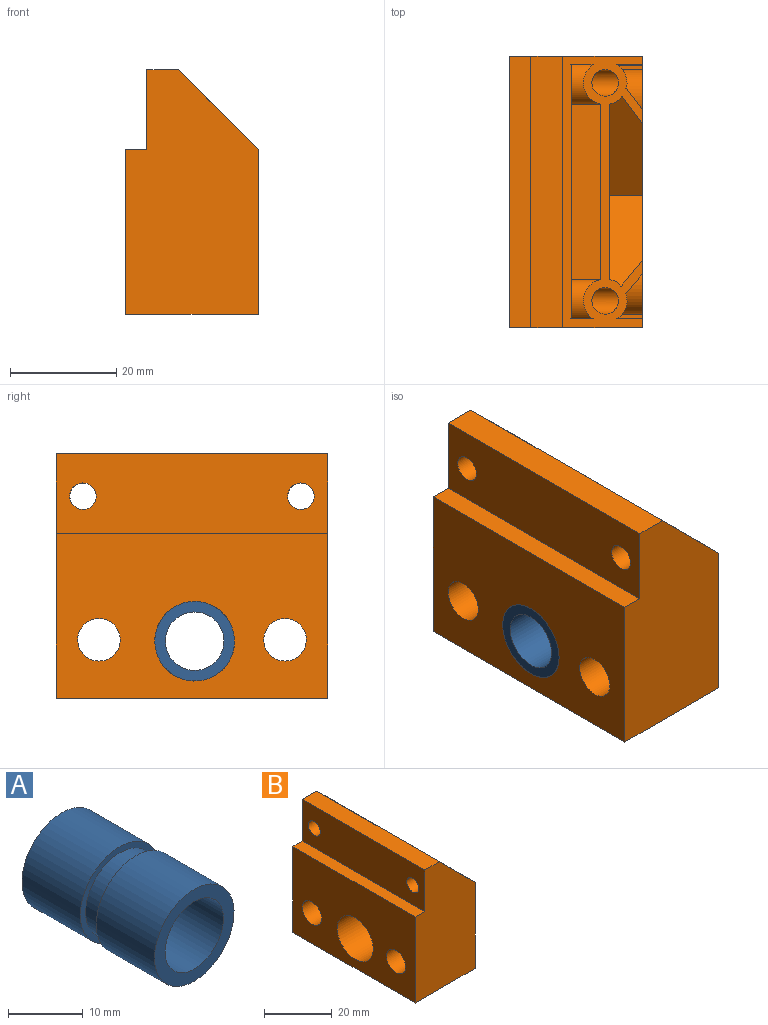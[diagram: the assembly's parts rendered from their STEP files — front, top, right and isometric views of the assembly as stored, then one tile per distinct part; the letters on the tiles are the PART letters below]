
ASSEMBLY  parts=2 mates=1
PART A: 8 faces, bbox 15x25x15 mm
  f0: cylinder r=7.5mm len=15mm, axis (0,1,0), area 518.4mm2, adj f1,f2
  f1: plane 15x15mm, normal (0,-1,0), area 44mm2, adj f0,f3
  f2: plane 15x15mm, normal (0,1,0), area 81.7mm2, adj f0,f7
  f3: cylinder r=6.5mm len=13mm, axis (0,1,0), area 122.5mm2, adj f1,f6
  f4: cylinder r=7.5mm len=15mm, axis (0,1,0), area 518.4mm2, adj f5,f6
  f5: plane 15x15mm, normal (0,-1,0), area 81.7mm2, adj f4,f7
  f6: plane 15x15mm, normal (0,1,0), area 44mm2, adj f3,f4
  f7: cylinder r=5.5mm len=25mm, axis (0,-1,0), area 863.9mm2, adj f2,f5
PART B: 77 faces, bbox 26.1x52.1x47.1 mm
  f0: plane 46x25mm, normal (0,1,0), area 977.5mm2, adj f1,f42,f43,f44,f48,f49,f69
  f1: plane 51x6mm, normal (0,0,1), area 306mm2, adj f0,f4,f48,f69
  f2: cylinder r=4.1mm len=16.5mm, axis (-1,0,0), area 85.8mm2, adj f8,f14,f51,f69
  f3: cylinder r=4.1mm len=16.5mm, axis (-1,0,0), area 80.5mm2, adj f7,f12,f22,f69
  f4: plane 46x25mm, normal (0,-1,0), area 977.5mm2, adj f1,f42,f43,f44,f48,f49,f69
  f5: cylinder r=2.5mm len=16.51mm, axis (-1,0,0), area 221.3mm2, adj f48,f69
  f6: cylinder r=2.5mm len=16.51mm, axis (-1,0,0), area 221.3mm2, adj f48,f69
  f7: plane 24.13x23.4mm, normal (0,-1,0), area 528.2mm2, adj f3,f16,f18,f22,f43,f66,f69
  f8: plane 24x23.4mm, normal (0,1,0), area 525.3mm2, adj f2,f17,f19,f43,f51,f64,f69
  f9: cylinder r=4.1mm len=15.41mm, axis (-1,0,0), area 36.8mm2, adj f11,f15,f21,f69
  f10: cylinder r=4.1mm len=15.57mm, axis (-1,0,0), area 40.5mm2, adj f11,f13,f21,f69
  f11: plane 32.96x13.2mm, normal (0,0,-1), area 435mm2, adj f9,f10,f21,f69
  f12: plane 23.4x18.93mm, normal (0,0.6,-0.8), area 515.6mm2, adj f3,f16,f18,f22,f43,f68,f69
  f13: plane 23.4x18.6mm, normal (0,-0.6,0.8), area 496.1mm2, adj f10,f15,f21,f32,f43,f52,f69
  f14: plane 23.4x17.16mm, normal (0,-0.64,-0.77), area 484.8mm2, adj f2,f17,f19,f43,f51,f67,f69
  f15: plane 23.4x17.01mm, normal (0,0.64,0.77), area 470.2mm2, adj f9,f13,f21,f32,f43,f52,f69
  f16: plane 23.34x18.15mm, normal (1,0,0), area 264.3mm2, adj f7,f12,f18,f20,f37,f62,f66,f68
  f17: plane 21.88x17.69mm, normal (1,0,0), area 247.1mm2, adj f8,f14,f19,f33,f34,f59,f64,f67
  f18: plane 10.57x4mm, normal (0,0,-1), area 42.3mm2, adj f7,f12,f16,f22
  f19: plane 10.41x4mm, normal (0,0,-1), area 41.6mm2, adj f8,f14,f17,f51
  f20: cylinder r=9.1mm len=23.4mm, axis (-1,0,0), area 296.6mm2, adj f16,f43,f62,f68
  f21: plane 35.61x7.8mm, normal (1,0,0), area 235.5mm2, adj f9,f10,f11,f13,f15,f52
  f22: plane 10.57x6.31mm, normal (1,0,0), area 36mm2, adj f3,f7,f12,f18
  f23: plane 8.38x5.32mm, normal (1,0,0), area 30.5mm2, adj f24,f25,f35,f58,f65
  f24: plane 23.4x8.38mm, normal (0,-1,0), area 196.1mm2, adj f23,f35,f43,f65
  f25: cylinder r=5.6mm len=23.4mm, axis (1,0,0), area 156.4mm2, adj f23,f43,f58,f65
  f26: plane 8.51x5.62mm, normal (1,0,0), area 31.8mm2, adj f27,f28,f50,f53,f63
  f27: plane 23.4x8.51mm, normal (0,1,0), area 199mm2, adj f26,f43,f50,f63
  f28: cylinder r=5.6mm len=23.4mm, axis (1,0,0), area 166.6mm2, adj f26,f43,f53,f63
  f29: plane 16.36x8.05mm, normal (1,0,0), area 70.5mm2, adj f30,f31,f38,f56,f57,f61
  f30: cylinder r=9.1mm len=23.4mm, axis (-1,0,0), area 282.8mm2, adj f29,f43,f56,f61
  f31: cylinder r=5.6mm len=23.4mm, axis (1,0,0), area 161.8mm2, adj f29,f43,f57,f61
  f32: plane 21.66x8.55mm, normal (1,0,0), area 92.6mm2, adj f13,f15,f52
  f33: cylinder r=9.1mm len=23.4mm, axis (-1,0,0), area 269.5mm2, adj f17,f43,f59,f67
  f34: cylinder r=5.6mm len=23.4mm, axis (1,0,0), area 378.5mm2, adj f17,f43,f59,f64
  f35: plane 23.4x5.32mm, normal (0,0,1), area 124.4mm2, adj f23,f24,f43,f58
  f36: plane 15.7x8.51mm, normal (1,0,0), area 62.5mm2, adj f39,f40,f41,f54,f55,f60
  f37: cylinder r=5.6mm len=23.4mm, axis (1,0,0), area 392.2mm2, adj f16,f43,f62,f66
  f38: plane 23.4x16.36mm, normal (0,0,1), area 382.9mm2, adj f29,f43,f56,f57
  f39: cylinder r=9.1mm len=23.4mm, axis (-1,0,0), area 308.5mm2, adj f36,f43,f55,f60
  f40: plane 23.4x15.7mm, normal (0,0,1), area 367.3mm2, adj f36,f43,f54,f55
  f41: cylinder r=5.6mm len=23.4mm, axis (1,0,0), area 165.5mm2, adj f36,f43,f54,f60
  f42: plane 51x31mm, normal (-1,0,0), area 1303.8mm2, adj f0,f4,f44,f45,f46,f47,f49
  f43: plane 51x31mm, normal (1,0,0), area 436.2mm2, adj f0,f4,f7,f8,f12,f13,f14,f15
  f44: plane 51x25mm, normal (0,0,-1), area 1275mm2, adj f0,f4,f42,f43
  f45: cylinder r=4mm len=25mm, axis (1,0,0), area 628.3mm2, adj f42,f43
  f46: cylinder r=4mm len=25mm, axis (1,0,0), area 628.3mm2, adj f42,f43
  f47: cylinder r=7.5mm len=25mm, axis (-1,0,0), area 1178.1mm2, adj f42,f43
  f48: plane 51x15mm, normal (-1,0,0), area 725.7mm2, adj f0,f1,f4,f5,f6,f49
  f49: plane 51x4mm, normal (0,0,1), area 204mm2, adj f0,f4,f42,f48
  f50: plane 23.4x5.62mm, normal (0,0,1), area 131.6mm2, adj f26,f27,f43,f53
  f51: plane 10.41x6.31mm, normal (1,0,0), area 36.6mm2, adj f2,f8,f14,f19
  f52: plane 21.66x4mm, normal (0,0,-1), area 86.6mm2, adj f13,f15,f21,f32
  f53: plane 23.4x3.85mm, normal (0,-1,0), area 90.2mm2, adj f26,f28,f43,f50
  f54: plane 23.4x3.86mm, normal (0,1,0), area 90.3mm2, adj f36,f40,f41,f43
  f55: plane 23.4x0.05mm, normal (0,-1,0), area 1.1mm2, adj f36,f39,f40,f43
  f56: plane 23.4x0.1mm, normal (0,1,0), area 2.4mm2, adj f29,f30,f38,f43
  f57: plane 23.4x3.82mm, normal (0,-1,0), area 89.5mm2, adj f29,f31,f38,f43
  f58: plane 23.4x3.91mm, normal (0,1,0), area 91.4mm2, adj f23,f25,f35,f43
  f59: plane 23.4x2.4mm, normal (0,0,1), area 56.1mm2, adj f17,f33,f34,f43
  f60: plane 23.4x2.39mm, normal (0,0,-1), area 56mm2, adj f36,f39,f41,f43
  f61: plane 23.4x3.53mm, normal (0,0,-1), area 82.6mm2, adj f29,f30,f31,f43
  f62: plane 23.4x3.32mm, normal (0,0,1), area 77.7mm2, adj f16,f20,f37,f43
  f63: plane 23.4x0.87mm, normal (0,0,-1), area 20.4mm2, adj f26,f27,f28,f43
  f64: plane 23.4x0.84mm, normal (0,0,1), area 19.8mm2, adj f8,f17,f34,f43
  f65: plane 23.4x0.89mm, normal (0,0,-1), area 20.9mm2, adj f23,f24,f25,f43
  f66: plane 23.4x0.83mm, normal (0,0,1), area 19.4mm2, adj f7,f16,f37,f43
  f67: plane 23.4x0.28mm, normal (0,-0.6,0.8), area 8.1mm2, adj f14,f17,f33,f43
  f68: plane 23.4x0.04mm, normal (0,0.64,0.77), area 1.2mm2, adj f12,f16,f20,f43
  f69: plane 52.05x16.05mm, normal (0.71,0,0.71), area 363.2mm2, adj f0,f1,f2,f3,f4,f5,f6,f7
  f70: plane 47.8x5.6mm, normal (1,0,0), area 229mm2, adj f71,f72,f73,f74,f75,f76
  f71: plane 47.8x6mm, normal (0,0,-1), area 286.8mm2, adj f69,f70,f72,f73
  f72: plane 10.11x4.11mm, normal (0,1,0), area 33.1mm2, adj f69,f70,f71,f76
  f73: plane 10.11x4.11mm, normal (0,-1,0), area 33.1mm2, adj f69,f70,f71,f75
  f74: plane 32.96x11.6mm, normal (0,0,1), area 382.3mm2, adj f69,f70,f75,f76
  f75: cylinder r=4.1mm len=11.6mm, axis (-1,0,0), area 89.2mm2, adj f69,f70,f73,f74
  f76: cylinder r=4.1mm len=11.6mm, axis (-1,0,0), area 89.2mm2, adj f69,f70,f72,f74
PLACE A rot(axis=(-0.58,0.58,0.58),120deg) t=(-13.23,-22.48,15.44)mm
PLACE B t=(-1.47,-35.04,4.7)mm
MATE fastened A.f0 <-> B.f20  axis (1,0,0) through (11.77,-22.48,15.44)mm
